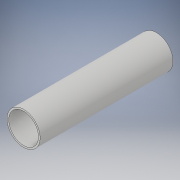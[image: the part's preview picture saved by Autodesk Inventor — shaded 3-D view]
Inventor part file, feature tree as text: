
AUTODESK INVENTOR PART (.ipt)
format: ipt  version: 2019 (Build 230136000, 136)  size: 98,816 bytes
history: native  units: mm
features: extrude x2, sketch x2
ambient origin geometry x8: Origin, YZ Plane, XZ Plane, XY Plane, X Axis, Y Axis, Z Axis, Center Point
bodies: Solid1 (feature_tree)
feature tree (4):
  extrude  "Extrusion1"  Depth=25.02mm TaperAngle=0.0deg
  extrude  "Extrusion2"  Depth=25.02mm TaperAngle=0.0deg
  sketch  "Sketch1"  dims[d0=6.24mm d1=25.02mm d2=0.0mm]
  sketch  "Sketch2"  dims[d3=5.6mm d4=25.02mm d5=0.0mm]
